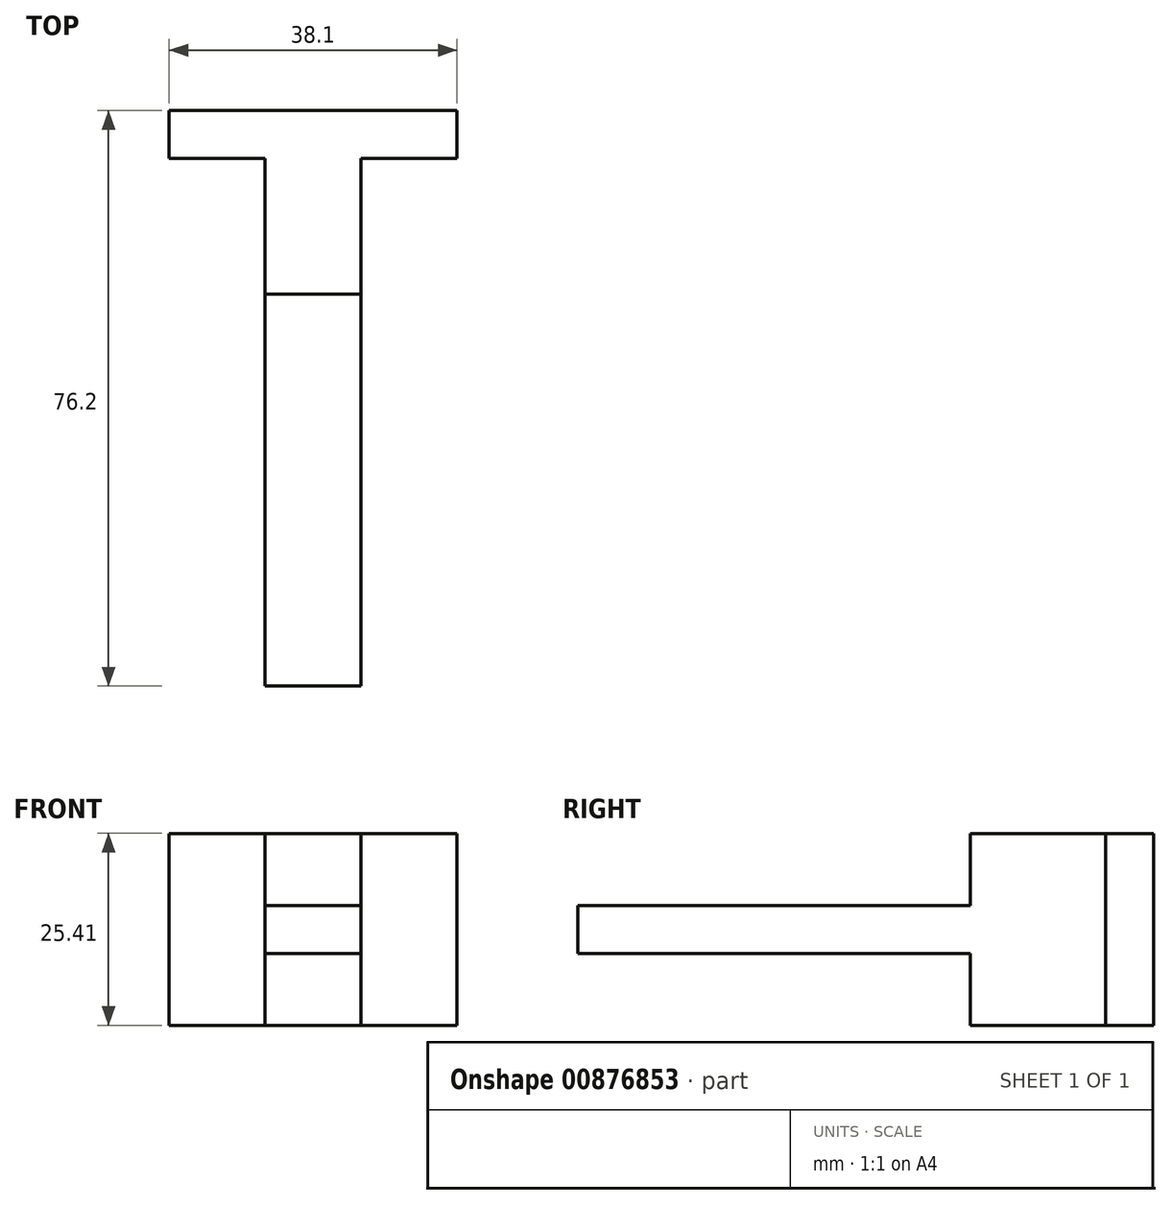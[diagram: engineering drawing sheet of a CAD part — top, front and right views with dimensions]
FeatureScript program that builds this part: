
annotation { "Feature Type Name" : "Feature", "Feature Type Description" : "" }
export const myFeature = defineFeature(function(context is Context, id is Id, definition is map)
    precondition{}
    {
        {
            var Q0;
            Q0=qCreatedBy(makeId("Top.planeOp"),FACE);
            var sketch = newSketch(context, id + "F0", { "sketchPlane" : qUnion([Q0])});
            skLineSegment(sketch, "E0.bottom", {"start": v(0, 2.94) * mm, "end": v(12.7, 2.94) * mm});
            skLineSegment(sketch, "E0.top", {"start": v(0, 79.14) * mm, "end": v(12.7, 79.14) * mm});
            skLineSegment(sketch, "E0.left", {"start": v(0, 2.94) * mm, "end": v(0, 79.14) * mm});
            skLineSegment(sketch, "E0.right", {"start": v(12.7, 2.94) * mm, "end": v(12.7, 79.14) * mm});
            skSolve(sketch);
        }
        {
            var Q0;
            Q0=makeQuery(id+"F0.imprint","IMPRINT",FACE,{"disambiguationData":[TD([[makeQuery(id+"F0.imprint","IMPRINT",EDGE,{"derivedFrom":sQuery(id+"F0.wireOp",EDGE,"E0.bottom")}),1.0]])]});
            extrude(context, id + "F1", {"entities" : qUnion([Q0]), "depth" : 6.35 * mm, "offsetDistance" : 25.4 * mm});
        }
        {
            var Q0;
            Q0=makeQuery(id+"F1.opExtrude","SWEPT_FACE",FACE,{"disambiguationData":[OSD([sQuery(id+"F0.wireOp",EDGE,"E0.left")])]});
            var sketch = newSketch(context, id + "F2", { "sketchPlane" : qUnion([Q0])});
            skLineSegment(sketch, "E1.bottom", {"start": v(-79.14, 15.88) * mm, "end": v(-72.8, 15.88) * mm});
            skLineSegment(sketch, "E1.top", {"start": v(-79.14, -9.53) * mm, "end": v(-72.8, -9.53) * mm});
            skLineSegment(sketch, "E1.left", {"start": v(-79.14, 15.87) * mm, "end": v(-79.14, -9.52) * mm});
            skLineSegment(sketch, "E1.right", {"start": v(-72.8, 15.88) * mm, "end": v(-72.8, -9.53) * mm});
            skSolve(sketch);
        }
        {
            var Q0;
            Q0 = qSketchRegion(id + "F2", true);
            extrude(context, id + "F3", {"entities" : qUnion([Q0]), "operationType" : NewBodyOperationType.ADD, "depth" : 12.7 * mm, "offsetDistance" : 25.4 * mm, "hasSecondDirection" : true, "secondDirectionOppositeDirection" : true, "secondDirectionDepth" : 25.4 * mm});
        }
        {
            var Q0;
            Q0=makeQuery(id+"F1.opExtrude","CAP_FACE",FACE,{"disambiguationData":[OSD([sQuery(id+"F0.wireOp",EDGE,"E0.bottom"),sQuery(id+"F0.wireOp",EDGE,"E0.top"),sQuery(id+"F0.wireOp",EDGE,"E0.left"),sQuery(id+"F0.wireOp",EDGE,"E0.right")])],"isStart":false});
            var sketch = newSketch(context, id + "F4", { "sketchPlane" : qUnion([Q0])});
            skLineSegment(sketch, "E2.bottom", {"start": v(0, 72.8) * mm, "end": v(12.7, 72.8) * mm});
            skLineSegment(sketch, "E2.top", {"start": v(0, 54.85) * mm, "end": v(12.7, 54.85) * mm});
            skLineSegment(sketch, "E2.left", {"start": v(0, 72.8) * mm, "end": v(0, 54.85) * mm});
            skLineSegment(sketch, "E2.right", {"start": v(12.7, 72.8) * mm, "end": v(12.7, 54.85) * mm});
            skSolve(sketch);
        }
        {
            var Q0;
            Q0 = qSketchRegion(id + "F4", true);
            extrude(context, id + "F5", {"entities" : qUnion([Q0]), "operationType" : NewBodyOperationType.ADD, "depth" : 9.52 * mm, "offsetDistance" : 25.4 * mm, "hasSecondDirection" : true, "secondDirectionOppositeDirection" : true, "secondDirectionDepth" : 15.88 * mm});
        }
    });
